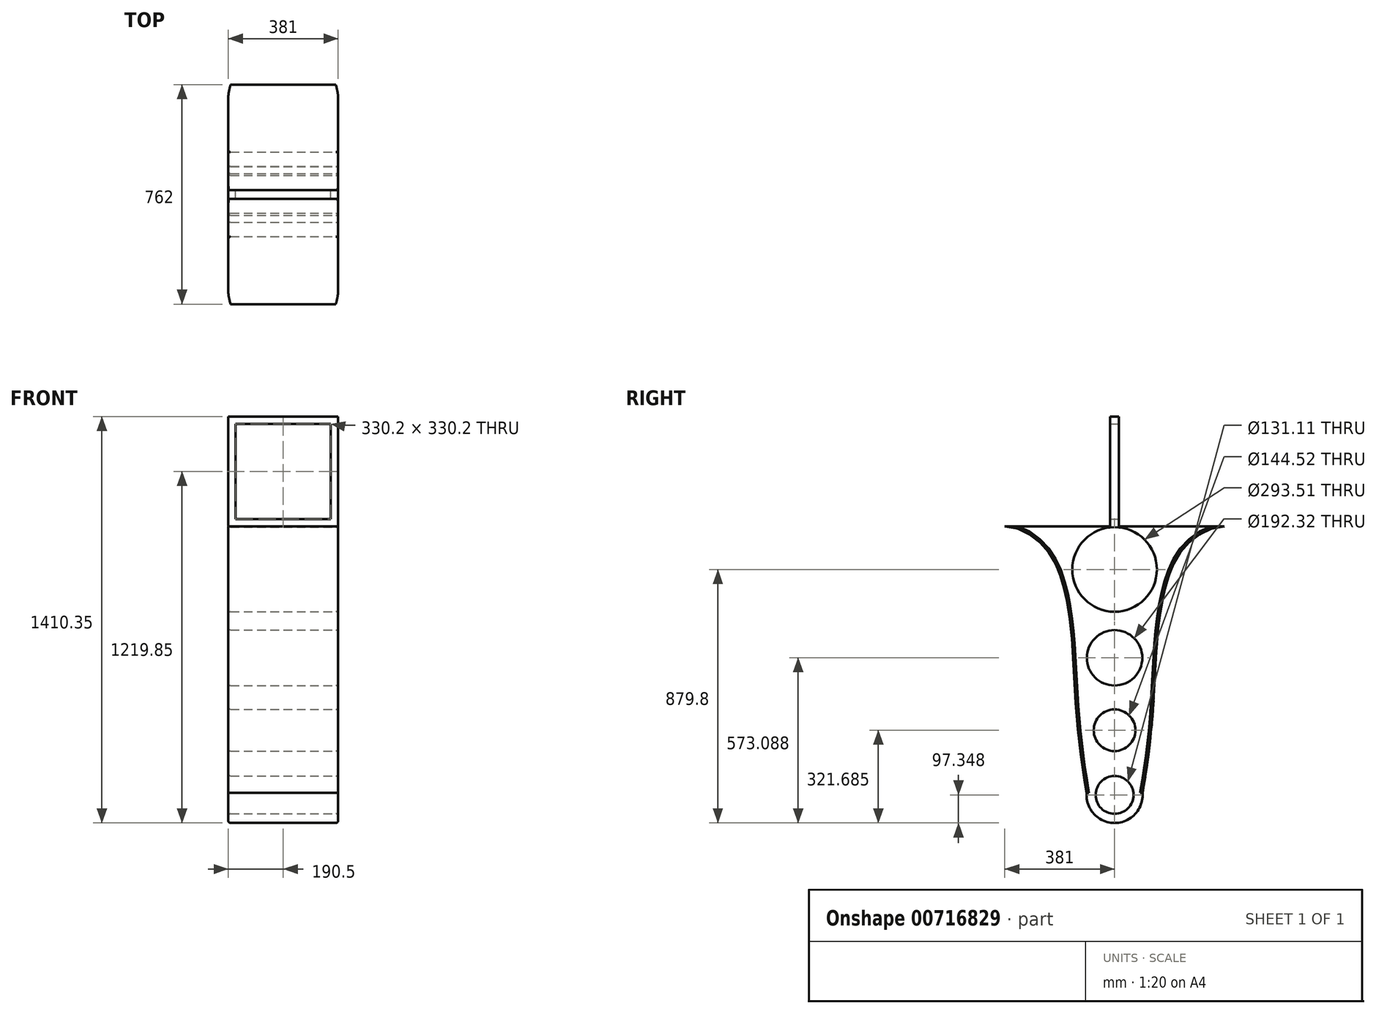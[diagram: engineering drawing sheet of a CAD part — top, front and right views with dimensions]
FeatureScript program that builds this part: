
annotation { "Feature Type Name" : "Feature", "Feature Type Description" : "" }
export const myFeature = defineFeature(function(context is Context, id is Id, definition is map)
    precondition{}
    {
        {
            assignVariable(context, id + "F0", {"name" : "h", "anyValue" : 30});
        }
        {
            var Q0;
            Q0=qCreatedBy(makeId("Front.planeOp"),FACE);
            var sketch = newSketch(context, id + "F1", { "sketchPlane" : qUnion([Q0])});
            skLineSegment(sketch, "E0.bottom", {"start": v(-165.1, -165.1) * mm, "end": v(165.1, -165.1) * mm});
            skLineSegment(sketch, "E0.top", {"start": v(-165.1, 165.1) * mm, "end": v(165.1, 165.1) * mm});
            skLineSegment(sketch, "E0.left", {"start": v(-165.1, -165.1) * mm, "end": v(-165.1, 165.1) * mm});
            skLineSegment(sketch, "E0.right", {"start": v(165.1, -165.1) * mm, "end": v(165.1, 165.1) * mm});
            skPoint(sketch, "E0.middle", {"position": v(0, 0) * mm});
            skLineSegment(sketch, "E1.bottom", {"start": v(-190.5, 190.5) * mm, "end": v(190.5, 190.5) * mm});
            skLineSegment(sketch, "E1.top", {"start": v(-190.5, -190.5) * mm, "end": v(190.5, -190.5) * mm});
            skLineSegment(sketch, "E1.left", {"start": v(-190.5, 190.5) * mm, "end": v(-190.5, -190.5) * mm});
            skLineSegment(sketch, "E1.right", {"start": v(190.5, 190.5) * mm, "end": v(190.5, -190.5) * mm});
            skSolve(sketch);
        }
        {
            var Q0;
            Q0=makeQuery(id+"F1.imprint","IMPRINT",FACE,{"disambiguationData":[TD([[makeQuery(id+"F1.imprint","IMPRINT",EDGE,{"derivedFrom":sQuery(id+"F1.wireOp",EDGE,"E0.bottom")}),-1.0]])]});
            extrude(context, id + "F2", {"entities" : qUnion([Q0]), "endBound" : BoundingType.SYMMETRIC, "depth" : (getVariable(context, 'h')) * mm, "offsetDistance" : 25.4 * mm});
        }
        {
            var Q0;
            Q0=makeQuery(id+"F2.opExtrude","SWEPT_FACE",FACE,{"disambiguationData":[OSD([sQuery(id+"F1.wireOp",EDGE,"E1.right")])]});
            var sketch = newSketch(context, id + "F3", { "sketchPlane" : qUnion([Q0])});
            skCircle(sketch, "E2", {"center": v(0, -340.05) * mm, "radius": 146.75 * mm});
            skPoint(sketch, "E2.centerSnap0", {"position": v(0, -190.5) * mm});
            skCircle(sketch, "E3", {"center": v(0, -898.17) * mm, "radius": 72.26 * mm});
            skCircle(sketch, "E4", {"center": v(0, -1122.5) * mm, "radius": 65.56 * mm});
            skFitSpline(sketch, "E5", {"points": [v(381, -190.5) * mm, v(218.03, -296.13) * mm, v(136.18, -775.97) * mm, v(97.11, -1115.72) * mm], "startDerivative": vector(-564.84, 0) * mm, "endDerivative": vector(-174.34, -1048.12) * mm});
            skLineSegment(sketch, "E6", {"start": v(-381, -190.5) * mm, "end": v(381, -190.5) * mm});
            skFitSpline(sketch, "E7.MirrorCS", {"points": [v(-381, -190.5) * mm, v(-218.03, -296.13) * mm, v(-136.18, -775.97) * mm, v(-97.11, -1115.72) * mm], "startDerivative": vector(564.84, 0) * mm, "endDerivative": vector(174.34, -1048.12) * mm});
            skArc(sketch, "E8", {"start": v(-97.11, -1115.72) * mm, "mid": v(0, -1219.85) * mm, "end": v(97.11, -1115.72) * mm});
            skCircle(sketch, "E9", {"center": v(0, -646.76) * mm, "radius": 96.16 * mm});
            skSolve(sketch);
        }
        {
            var Q0;
            Q0=makeQuery(id+"F3.imprint","IMPRINT",FACE,{"disambiguationData":[TD([[makeQuery(id+"F3.imprint","IMPRINT",EDGE,{"derivedFrom":sQuery(id+"F3.wireOp",EDGE,"E2")}),-1.0]])]});
            var Q1;
            Q1=makeQuery(id+"F2.opExtrude","SWEPT_FACE",FACE,{"disambiguationData":[OSD([sQuery(id+"F1.wireOp",EDGE,"E1.left")])]});
            extrude(context, id + "F4", {"entities" : qUnion([Q0]), "operationType" : NewBodyOperationType.ADD, "endBound" : BoundingType.UP_TO_SURFACE, "oppositeDirection" : true, "depth" : 25.4 * mm, "endBoundEntityFace" : qUnion([Q1]), "offsetDistance" : 25.4 * mm});
        }
        {
            var Q0;
            Q0=makeQuery(id+"F4.opExtrude","CAP_EDGE",EDGE,{"disambiguationData":[OSD([sQuery(id+"F3.wireOp",EDGE,"E7.MirrorCS")])],"isStart":true});
            var Q1;
            Q1=makeQuery(id+"F4.opExtrude","CAP_EDGE",EDGE,{"disambiguationData":[OSD([sQuery(id+"F3.wireOp",EDGE,"E8")])],"isStart":true});
            var Q2;
            Q2=makeQuery(id+"F4.opExtrude","CAP_EDGE",EDGE,{"disambiguationData":[OSD([sQuery(id+"F3.wireOp",EDGE,"E5")])],"isStart":true});
            var Q3;
            Q3=makeQuery(id+"F4.opExtrude","CAP_EDGE",EDGE,{"disambiguationData":[OSD([sQuery(id+"F3.wireOp",EDGE,"E7.MirrorCS")])],"isStart":false});
            var Q4;
            Q4=makeQuery(id+"F4.opExtrude","CAP_EDGE",EDGE,{"disambiguationData":[OSD([sQuery(id+"F3.wireOp",EDGE,"E5")])],"isStart":false});
            var Q5;
            Q5=makeQuery(id+"F4.opExtrude","CAP_EDGE",EDGE,{"disambiguationData":[OSD([sQuery(id+"F3.wireOp",EDGE,"E8")])],"isStart":false});
            fillet(context, id + "F5", {"entities" : qUnion([Q0, Q1, Q2, Q3, Q4, Q5]), "radius" : 8 * mm, "tangentPropagation" : true, "allowEdgeOverflow" : false});
        }
        {
            var Q0;
            Q0=makeQuery(id+"F4.opExtrude","CAP_EDGE",EDGE,{"disambiguationData":[OSD([sQuery(id+"F3.wireOp",EDGE,"E4")])],"isStart":false});
            var Q1;
            Q1=makeQuery(id+"F4.opExtrude","CAP_EDGE",EDGE,{"disambiguationData":[OSD([sQuery(id+"F3.wireOp",EDGE,"E3")])],"isStart":false});
            var Q2;
            Q2=makeQuery(id+"F4.opExtrude","CAP_EDGE",EDGE,{"disambiguationData":[OSD([sQuery(id+"F3.wireOp",EDGE,"E9")])],"isStart":false});
            var Q3;
            Q3=makeQuery(id+"F4.opExtrude","CAP_EDGE",EDGE,{"disambiguationData":[OSD([sQuery(id+"F3.wireOp",EDGE,"E2")])],"isStart":false});
            var Q4;
            Q4=makeQuery(id+"F4.opExtrude","CAP_EDGE",EDGE,{"disambiguationData":[OSD([sQuery(id+"F3.wireOp",EDGE,"E2")])],"isStart":true});
            var Q5;
            Q5=makeQuery(id+"F4.opExtrude","CAP_EDGE",EDGE,{"disambiguationData":[OSD([sQuery(id+"F3.wireOp",EDGE,"E9")])],"isStart":true});
            var Q6;
            Q6=makeQuery(id+"F4.opExtrude","CAP_EDGE",EDGE,{"disambiguationData":[OSD([sQuery(id+"F3.wireOp",EDGE,"E3")])],"isStart":true});
            var Q7;
            Q7=makeQuery(id+"F4.opExtrude","CAP_EDGE",EDGE,{"disambiguationData":[OSD([sQuery(id+"F3.wireOp",EDGE,"E4")])],"isStart":true});
            fillet(context, id + "F6", {"entities" : qUnion([Q0, Q1, Q2, Q3, Q4, Q5, Q6, Q7]), "radius" : 8 * mm, "tangentPropagation" : true, "allowEdgeOverflow" : false});
        }
    });
